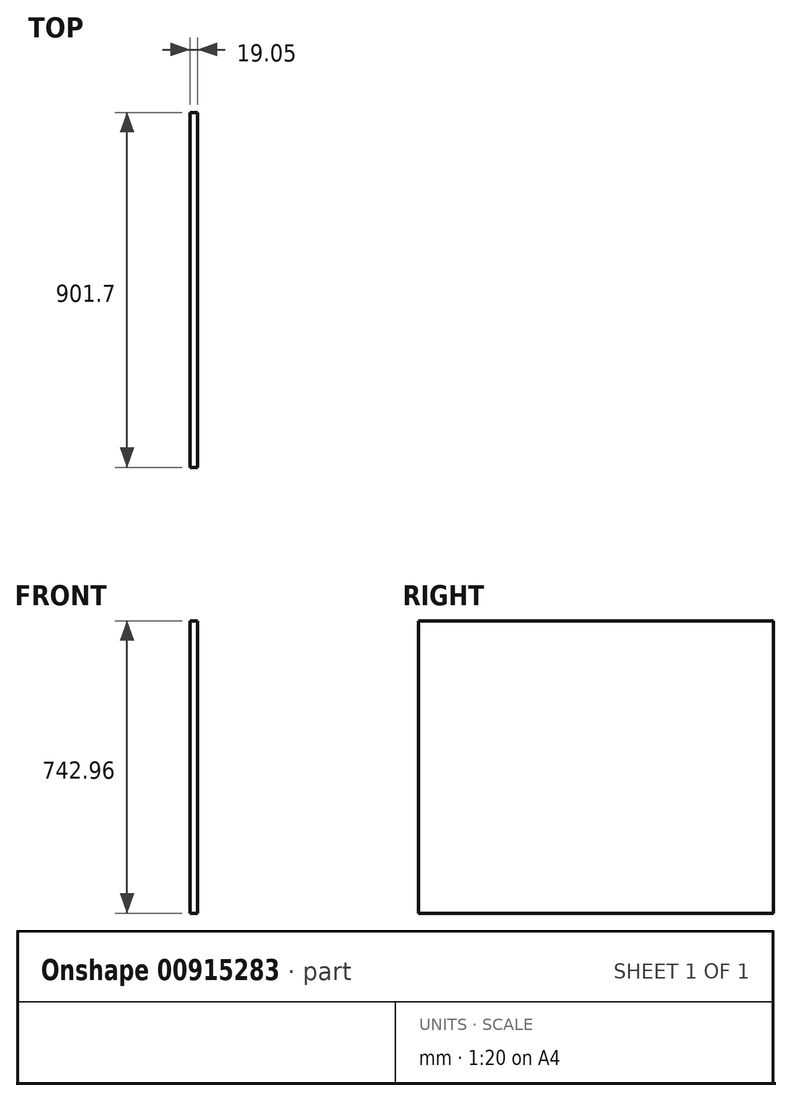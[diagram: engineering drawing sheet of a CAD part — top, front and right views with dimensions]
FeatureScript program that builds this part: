
annotation { "Feature Type Name" : "Feature", "Feature Type Description" : "" }
export const myFeature = defineFeature(function(context is Context, id is Id, definition is map)
    precondition{}
    {
        {
            var Q0;
            Q0=qCreatedBy(makeId("Right.planeOp"),FACE);
            var sketch = newSketch(context, id + "F0", { "sketchPlane" : qUnion([Q0])});
            skLineSegment(sketch, "E0.bottom", {"start": v(450.85, 371.48) * mm, "end": v(-450.85, 371.48) * mm});
            skLineSegment(sketch, "E0.top", {"start": v(450.85, -371.48) * mm, "end": v(-450.85, -371.48) * mm});
            skLineSegment(sketch, "E0.left", {"start": v(450.85, 371.48) * mm, "end": v(450.85, -371.48) * mm});
            skLineSegment(sketch, "E0.right", {"start": v(-450.85, 371.48) * mm, "end": v(-450.85, -371.48) * mm});
            skPoint(sketch, "E0.middle", {"position": v(0, 0) * mm});
            skSolve(sketch);
        }
        {
            var Q0;
            Q0=makeQuery(id+"F0.imprint","IMPRINT",FACE,{"disambiguationData":[TD([[makeQuery(id+"F0.imprint","IMPRINT",EDGE,{"derivedFrom":sQuery(id+"F0.wireOp",EDGE,"E0.bottom")}),1.0]])]});
            extrude(context, id + "F1", {"entities" : qUnion([Q0]), "depth" : 19.05 * mm, "offsetDistance" : 25.4 * mm});
        }
    });
